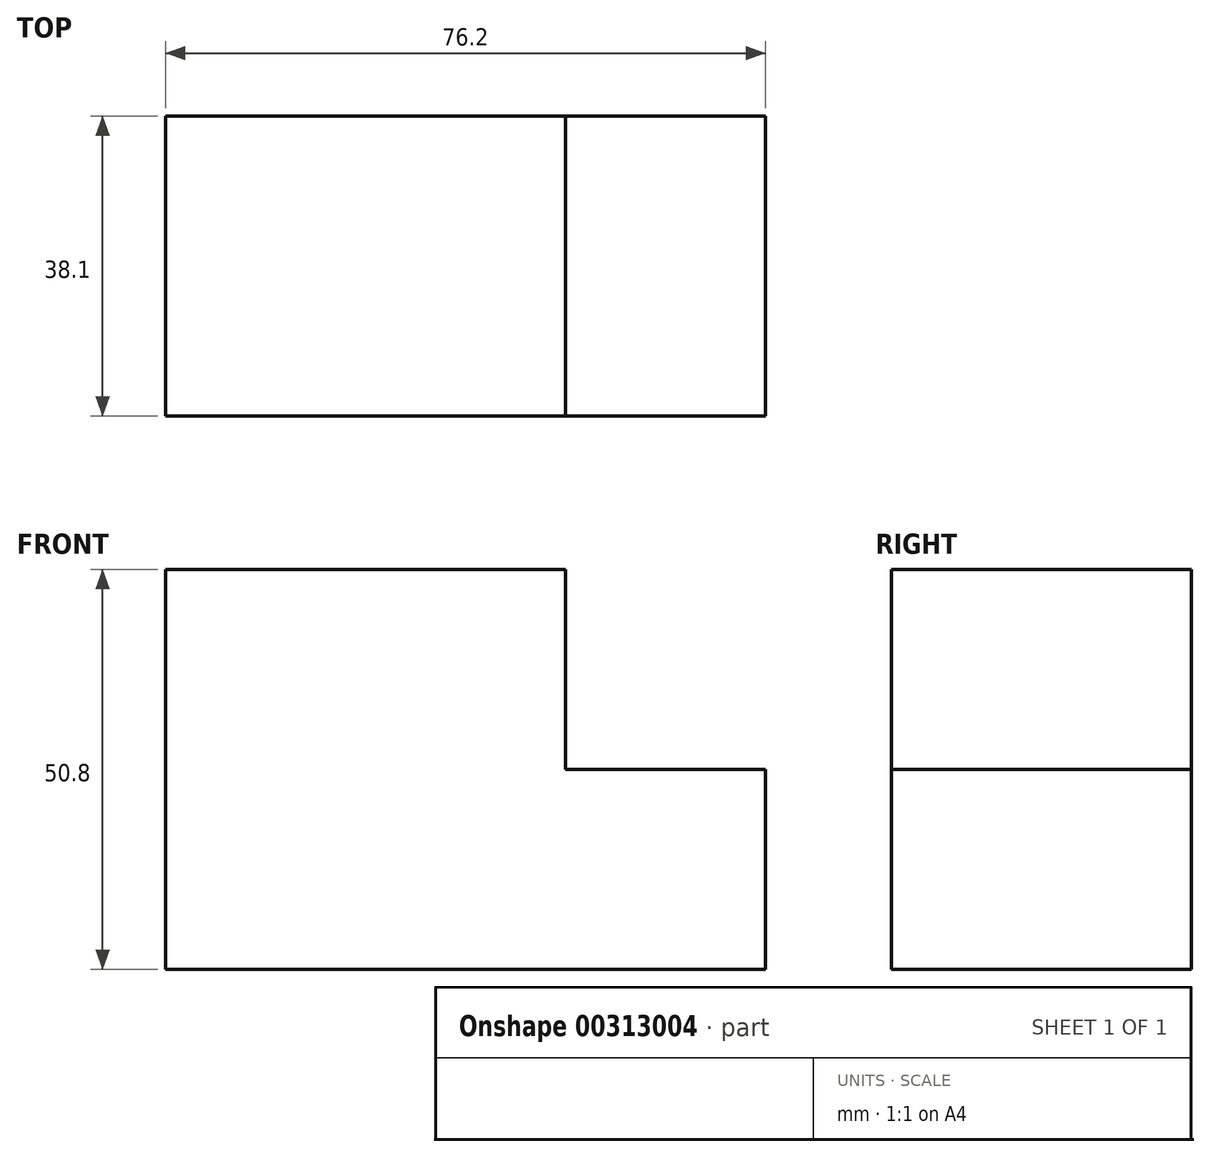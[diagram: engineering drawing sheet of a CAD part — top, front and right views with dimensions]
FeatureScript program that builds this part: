
annotation { "Feature Type Name" : "Feature", "Feature Type Description" : "" }
export const myFeature = defineFeature(function(context is Context, id is Id, definition is map)
    precondition{}
    {
        {
            var Q0;
            Q0=qCreatedBy(makeId("Front.planeOp"),FACE);
            var sketch = newSketch(context, id + "F0", { "sketchPlane" : qUnion([Q0])});
            skLineSegment(sketch, "E0", {"start": v(-41.14, -35.4) * mm, "end": v(35.06, -35.4) * mm});
            skLineSegment(sketch, "E1", {"start": v(35.06, -35.4) * mm, "end": v(35.06, -10) * mm});
            skLineSegment(sketch, "E2", {"start": v(35.06, -10) * mm, "end": v(9.66, -10) * mm});
            skLineSegment(sketch, "E3", {"start": v(9.66, -10) * mm, "end": v(9.66, 15.4) * mm});
            skLineSegment(sketch, "E4", {"start": v(9.66, 15.4) * mm, "end": v(-41.14, 15.4) * mm});
            skLineSegment(sketch, "E5", {"start": v(-41.14, 15.4) * mm, "end": v(-41.14, -35.4) * mm});
            skSolve(sketch);
        }
        {
            var Q0;
            Q0=makeQuery(id+"F0.imprint","IMPRINT",FACE,{"disambiguationData":[TD([[makeQuery(id+"F0.imprint","IMPRINT",EDGE,{"derivedFrom":sQuery(id+"F0.wireOp",EDGE,"E0")}),1.0]])]});
            extrude(context, id + "F1", {"entities" : qUnion([Q0]), "depth" : 38.1 * mm});
        }
    });
